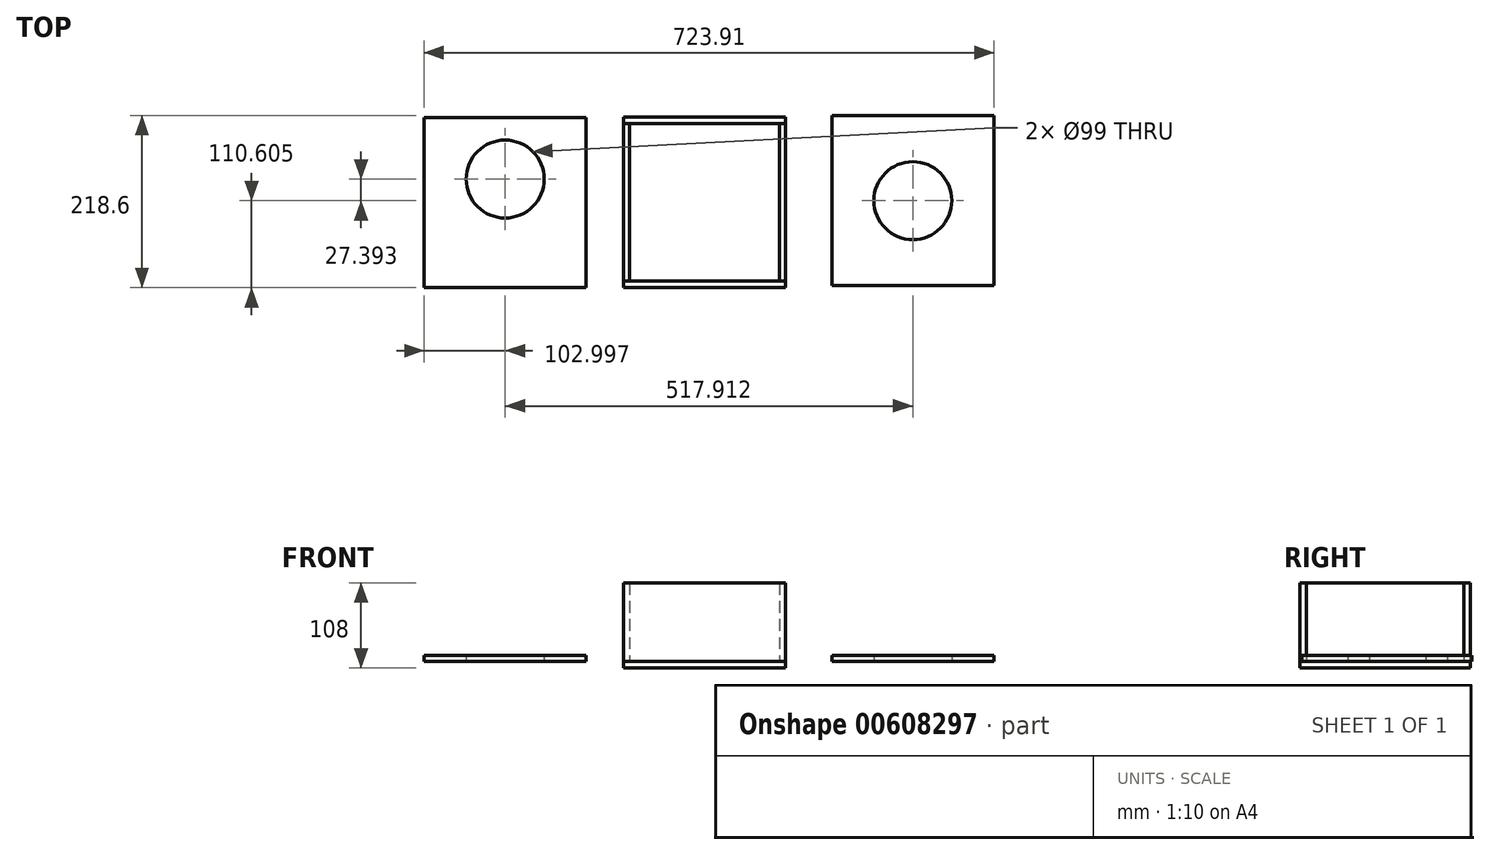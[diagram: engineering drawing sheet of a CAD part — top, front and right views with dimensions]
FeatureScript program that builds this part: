
annotation { "Feature Type Name" : "Feature", "Feature Type Description" : "" }
export const myFeature = defineFeature(function(context is Context, id is Id, definition is map)
    precondition{}
    {
        {
            assignVariable(context, id + "F0", {"name" : "thikness", "anyValue" : 8});
        }
        {
            assignVariable(context, id + "F1", {"name" : "height", "anyValue" : 100});
        }
        {
            var Q0;
            Q0=qCreatedBy(makeId("Top.planeOp"),FACE);
            var sketch = newSketch(context, id + "F2", { "sketchPlane" : qUnion([Q0])});
            skLineSegment(sketch, "E0.bottom", {"start": v(-102.04, 88.26) * mm, "end": v(87.96, 88.26) * mm});
            skLineSegment(sketch, "E0.top", {"start": v(-102.04, -111.74) * mm, "end": v(87.96, -111.74) * mm});
            skLineSegment(sketch, "E0.left", {"start": v(-102.04, 88.26) * mm, "end": v(-102.04, -111.74) * mm});
            skLineSegment(sketch, "E0.right", {"start": v(87.96, 88.26) * mm, "end": v(87.96, -111.74) * mm});
            skLineSegment(sketch, "E1.0", {"start": v(-110.04, 96.26) * mm, "end": v(-110.04, -119.74) * mm});
            skLineSegment(sketch, "E1.1", {"start": v(-110.04, 96.26) * mm, "end": v(95.96, 96.26) * mm});
            skLineSegment(sketch, "E1.2", {"start": v(95.96, 96.26) * mm, "end": v(95.96, -119.74) * mm});
            skLineSegment(sketch, "E1.3", {"start": v(-110.04, -119.74) * mm, "end": v(95.96, -119.74) * mm});
            skLineSegment(sketch, "E2", {"start": v(-102.04, 88.26) * mm, "end": v(-110.04, 88.26) * mm});
            skLineSegment(sketch, "E3", {"start": v(87.96, 88.26) * mm, "end": v(95.96, 88.26) * mm});
            skLineSegment(sketch, "E4", {"start": v(-102.04, -111.74) * mm, "end": v(-110.04, -111.74) * mm});
            skLineSegment(sketch, "E5", {"start": v(87.96, -111.74) * mm, "end": v(95.96, -111.74) * mm});
            skLineSegment(sketch, "E6.bottom", {"start": v(154.6, 98.34) * mm, "end": v(360.6, 98.34) * mm});
            skLineSegment(sketch, "E6.top", {"start": v(154.6, -117.66) * mm, "end": v(360.6, -117.66) * mm});
            skLineSegment(sketch, "E6.left", {"start": v(154.6, 98.34) * mm, "end": v(154.6, -117.66) * mm});
            skLineSegment(sketch, "E6.right", {"start": v(360.6, 98.34) * mm, "end": v(360.6, -117.66) * mm});
            skLineSegment(sketch, "E7.bottom", {"start": v(-157.3, 95.74) * mm, "end": v(-363.3, 95.74) * mm});
            skLineSegment(sketch, "E7.top", {"start": v(-157.3, -120.26) * mm, "end": v(-363.3, -120.26) * mm});
            skLineSegment(sketch, "E7.left", {"start": v(-157.3, 95.74) * mm, "end": v(-157.3, -120.26) * mm});
            skLineSegment(sketch, "E7.right", {"start": v(-363.3, 95.74) * mm, "end": v(-363.3, -120.26) * mm});
            skCircle(sketch, "E8", {"center": v(-260.3, 17.74) * mm, "radius": 49.5 * mm});
            skCircle(sketch, "E9", {"center": v(257.6, -9.66) * mm, "radius": 49.5 * mm});
            skSolve(sketch);
        }
        {
            var Q0;
            Q0=makeQuery(id+"F2.imprint","IMPRINT",FACE,{"disambiguationData":[TD([[makeQuery(id+"F2.imprint","IMPRINT",EDGE,{"derivedFrom":sQuery(id+"F2.wireOp",EDGE,"E0.bottom")}),1.0]])]});
            var Q1;
            Q1=makeQuery(id+"F2.imprint","IMPRINT",FACE,{"disambiguationData":[TD([[makeQuery(id+"F2.imprint","IMPRINT",EDGE,{"derivedFrom":sQuery(id+"F2.wireOp",EDGE,"E0.top")}),-1.0]])]});
            extrude(context, id + "F3", {"entities" : qUnion([Q0, Q1]), "depth" : (getVariable(context, 'height')) * mm, "offsetDistance" : 25 * mm});
        }
        {
            var Q0;
            Q0=makeQuery(id+"F2.imprint","IMPRINT",FACE,{"disambiguationData":[TD([[makeQuery(id+"F2.imprint","IMPRINT",EDGE,{"derivedFrom":sQuery(id+"F2.wireOp",EDGE,"E0.left")}),-1.0]])]});
            var Q1;
            Q1=makeQuery(id+"F2.imprint","IMPRINT",FACE,{"disambiguationData":[TD([[makeQuery(id+"F2.imprint","IMPRINT",EDGE,{"derivedFrom":sQuery(id+"F2.wireOp",EDGE,"E0.right")}),1.0]])]});
            extrude(context, id + "F4", {"entities" : qUnion([Q0, Q1]), "depth" : (getVariable(context, 'height')) * mm, "offsetDistance" : 25 * mm});
        }
        {
            var Q0;
            Q0=makeQuery(id+"F2.imprint","IMPRINT",FACE,{"disambiguationData":[TD([[makeQuery(id+"F2.imprint","IMPRINT",EDGE,{"derivedFrom":sQuery(id+"F2.wireOp",EDGE,"E0.right")}),1.0]])]});
            var Q1;
            Q1=makeQuery(id+"F2.imprint","IMPRINT",FACE,{"disambiguationData":[TD([[makeQuery(id+"F2.imprint","IMPRINT",EDGE,{"derivedFrom":sQuery(id+"F2.wireOp",EDGE,"E0.bottom")}),1.0]])]});
            var Q2;
            Q2=makeQuery(id+"F2.imprint","IMPRINT",FACE,{"disambiguationData":[TD([[makeQuery(id+"F2.imprint","IMPRINT",EDGE,{"derivedFrom":sQuery(id+"F2.wireOp",EDGE,"E0.left")}),-1.0]])]});
            var Q3;
            Q3=makeQuery(id+"F2.imprint","IMPRINT",FACE,{"disambiguationData":[TD([[makeQuery(id+"F2.imprint","IMPRINT",EDGE,{"derivedFrom":sQuery(id+"F2.wireOp",EDGE,"E0.top")}),-1.0]])]});
            var Q4;
            Q4=makeQuery(id+"F2.imprint","IMPRINT",FACE,{"disambiguationData":[TD([[makeQuery(id+"F2.imprint","IMPRINT",EDGE,{"derivedFrom":sQuery(id+"F2.wireOp",EDGE,"E0.bottom")}),-1.0]])]});
            var Q5;
            Q5=sQuery(id+"F2.wireOp",EDGE,"E1.2");
            var Q6;
            Q6=sQuery(id+"F2.wireOp",EDGE,"E1.3");
            var Q7;
            Q7=sQuery(id+"F2.wireOp",EDGE,"E1.0");
            var Q8;
            Q8=sQuery(id+"F2.wireOp",EDGE,"E1.1");
            extrude(context, id + "F5", {"entities" : qUnion([Q0, Q1, Q2, Q3, Q4]), "surfaceEntities" : qUnion([Q5, Q6, Q7, Q8]), "oppositeDirection" : true, "depth" : getVariable(context, 'thikness') * mm, "offsetDistance" : 25 * mm});
        }
        {
            var Q0;
            Q0=makeQuery(id+"F2.imprint","IMPRINT",FACE,{"disambiguationData":[TD([[makeQuery(id+"F2.imprint","IMPRINT",EDGE,{"derivedFrom":sQuery(id+"F2.wireOp",EDGE,"E7.bottom")}),1.0]])]});
            extrude(context, id + "F6", {"entities" : qUnion([Q0]), "depth" : getVariable(context, 'thikness') * mm, "offsetDistance" : 25 * mm});
        }
        {
            var Q0;
            Q0=makeQuery(id+"F2.imprint","IMPRINT",FACE,{"disambiguationData":[TD([[makeQuery(id+"F2.imprint","IMPRINT",EDGE,{"derivedFrom":sQuery(id+"F2.wireOp",EDGE,"E6.bottom")}),-1.0]])]});
            extrude(context, id + "F7", {"entities" : qUnion([Q0]), "depth" : getVariable(context, 'thikness') * mm, "offsetDistance" : 25 * mm});
        }
    });
